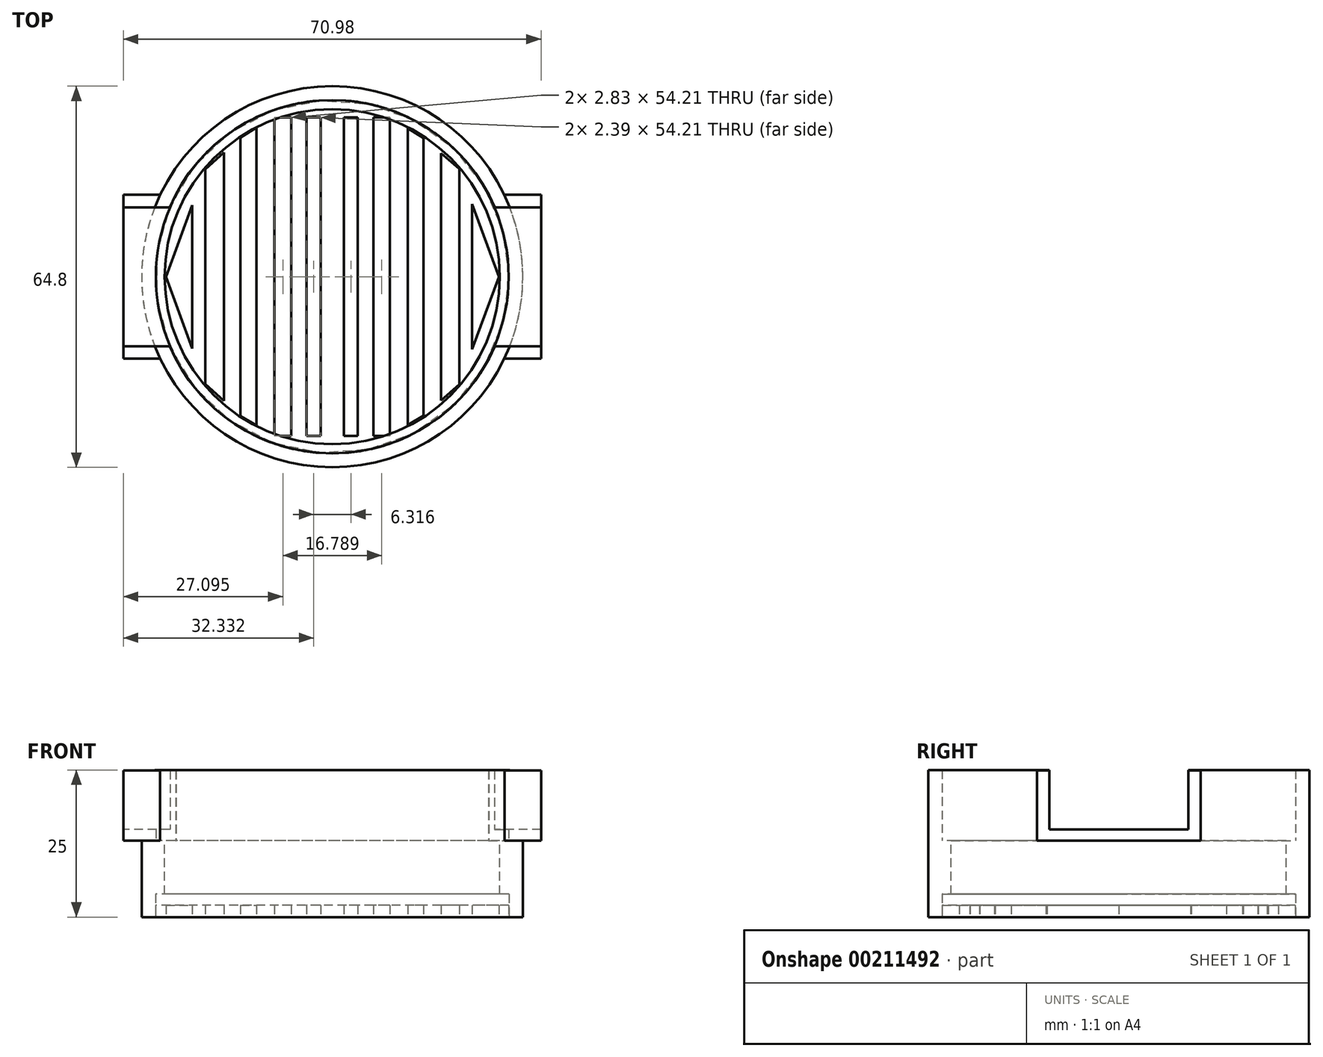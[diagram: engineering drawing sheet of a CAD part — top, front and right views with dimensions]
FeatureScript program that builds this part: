
annotation { "Feature Type Name" : "Feature", "Feature Type Description" : "" }
export const myFeature = defineFeature(function(context is Context, id is Id, definition is map)
    precondition{}
    {
        {
            var Q0;
            Q0=qCreatedBy(makeId("Top.planeOp"),FACE);
            var sketch = newSketch(context, id + "F0", { "sketchPlane" : qUnion([Q0])});
            skCircle(sketch, "E0", {"center": v(0, 0) * mm, "radius": 30 * mm});
            skLineSegment(sketch, "E1.top", {"start": v(1.96, -29.94) * mm, "end": v(-1.96, -29.94) * mm});
            skLineSegment(sketch, "E2.top", {"start": v(-6.98, -29.18) * mm, "end": v(-4.35, -29.18) * mm});
            skPoint(sketch, "E2.middle", {"position": v(-5.67, 0) * mm});
            skLineSegment(sketch, "E3.top", {"start": v(6.98, -29.18) * mm, "end": v(4.35, -29.18) * mm});
            skPoint(sketch, "E3.middle", {"position": v(5.67, 0) * mm});
            skLineSegment(sketch, "E4.top", {"start": v(-12.86, -27.1) * mm, "end": v(-9.8, -27.1) * mm});
            skLineSegment(sketch, "E4.right", {"start": v(-9.8, 27.1) * mm, "end": v(-9.8, -27.1) * mm});
            skPoint(sketch, "E4.middle", {"position": v(-11.33, 0) * mm});
            skLineSegment(sketch, "E5.top", {"start": v(12.86, -27.1) * mm, "end": v(9.8, -27.1) * mm});
            skLineSegment(sketch, "E5.right", {"start": v(9.8, 27.1) * mm, "end": v(9.8, -27.1) * mm});
            skPoint(sketch, "E5.middle", {"position": v(11.33, 0) * mm});
            skPoint(sketch, "E5.cornerSnap0", {"position": v(-11.33, 27.1) * mm});
            skPoint(sketch, "E6.middle", {"position": v(-17, 0) * mm});
            skPoint(sketch, "E7.middle", {"position": v(17, 0) * mm});
            skPoint(sketch, "E8.middle", {"position": v(22.67, 0) * mm});
            skPoint(sketch, "E9.middle", {"position": v(-22.67, 0) * mm});
            skLineSegment(sketch, "E10.top", {"start": v(-18.41, -23.69) * mm, "end": v(-15.6, -23.69) * mm});
            skLineSegment(sketch, "E10.right", {"start": v(-15.6, 23.69) * mm, "end": v(-15.6, -23.69) * mm});
            skLineSegment(sketch, "E11.top", {"start": v(-23.8, -18.28) * mm, "end": v(-21.55, -18.28) * mm});
            skLineSegment(sketch, "E11.right", {"start": v(-21.55, 18.28) * mm, "end": v(-21.55, -18.28) * mm});
            skLineSegment(sketch, "E12.top", {"start": v(18.49, -23.63) * mm, "end": v(15.52, -23.63) * mm});
            skLineSegment(sketch, "E12.right", {"start": v(15.52, 23.63) * mm, "end": v(15.52, -23.63) * mm});
            skLineSegment(sketch, "E13.top", {"start": v(23.77, -18.3) * mm, "end": v(21.57, -18.3) * mm});
            skLineSegment(sketch, "E13.right", {"start": v(21.57, 18.3) * mm, "end": v(21.57, -18.3) * mm});
            skLineSegment(sketch, "E14", {"start": v(21.57, -18.3) * mm, "end": v(15.52, -23.63) * mm});
            skLineSegment(sketch, "E15", {"start": v(15.52, -23.63) * mm, "end": v(9.8, -27.1) * mm});
            skLineSegment(sketch, "E16", {"start": v(9.8, -27.1) * mm, "end": v(-9.8, -27.1) * mm});
            skLineSegment(sketch, "E17", {"start": v(-15.6, -23.69) * mm, "end": v(-9.8, -27.1) * mm});
            skLineSegment(sketch, "E18", {"start": v(-15.6, -23.69) * mm, "end": v(-21.55, -18.28) * mm});
            skPoint(sketch, "E19.endSnap0", {"position": v(-12.86, 0) * mm});
            skLineSegment(sketch, "E20", {"start": v(23.77, -12.35) * mm, "end": v(23.77, 12.35) * mm});
            skLineSegment(sketch, "E21", {"start": v(28.3, 0) * mm, "end": v(23.77, 12.35) * mm});
            skLineSegment(sketch, "E22", {"start": v(28.3, 0) * mm, "end": v(23.77, -12.35) * mm});
            skLineSegment(sketch, "E23", {"start": v(18.49, 21.02) * mm, "end": v(18.49, -21.02) * mm});
            skLineSegment(sketch, "E24", {"start": v(12.86, 25.24) * mm, "end": v(12.86, -25.24) * mm});
            skLineSegment(sketch, "E25", {"start": v(6.98, 27.1) * mm, "end": v(6.98, -27.1) * mm});
            skLineSegment(sketch, "E26", {"start": v(-23.8, 12.19) * mm, "end": v(-23.8, -12.19) * mm});
            skLineSegment(sketch, "E27", {"start": v(-18.41, 21.13) * mm, "end": v(-18.41, -21.13) * mm});
            skLineSegment(sketch, "E28", {"start": v(-12.86, 25.4) * mm, "end": v(-12.86, -25.3) * mm});
            skPoint(sketch, "E28.startSnap0", {"position": v(-12.7, 25.4) * mm});
            skLineSegment(sketch, "E29", {"start": v(-6.98, 27.1) * mm, "end": v(-6.98, -27.1) * mm});
            skLineSegment(sketch, "E30", {"start": v(-1.96, -27.1) * mm, "end": v(-1.96, 27.1) * mm});
            skLineSegment(sketch, "E31", {"start": v(1.96, 27.1) * mm, "end": v(1.96, -27.1) * mm});
            skLineSegment(sketch, "E32", {"start": v(-28.27, 0) * mm, "end": v(-23.8, 12.19) * mm});
            skLineSegment(sketch, "E33", {"start": v(-28.27, 0) * mm, "end": v(-23.8, -12.19) * mm});
            skLineSegment(sketch, "E34", {"start": v(21.57, 18.3) * mm, "end": v(18.49, 21.02) * mm});
            skLineSegment(sketch, "E35", {"start": v(-21.55, 18.28) * mm, "end": v(-18.41, 21.13) * mm});
            skLineSegment(sketch, "E36", {"start": v(15.52, 23.63) * mm, "end": v(12.86, 25.24) * mm});
            skLineSegment(sketch, "E37", {"start": v(-15.6, 23.69) * mm, "end": v(-12.86, 25.4) * mm});
            skLineSegment(sketch, "E38", {"start": v(9.8, 27.1) * mm, "end": v(6.98, 27.1) * mm});
            skLineSegment(sketch, "E39", {"start": v(-9.8, 27.1) * mm, "end": v(-6.98, 27.1) * mm});
            skLineSegment(sketch, "E40", {"start": v(4.35, 27.1) * mm, "end": v(1.96, 27.1) * mm});
            skLineSegment(sketch, "E41", {"start": v(-1.96, 27.1) * mm, "end": v(-4.35, 27.1) * mm});
            skLineSegment(sketch, "E42", {"start": v(4.35, 27.1) * mm, "end": v(4.35, -27.1) * mm});
            skLineSegment(sketch, "E43", {"start": v(-4.35, 27.1) * mm, "end": v(-4.35, -27.1) * mm});
            skSolve(sketch);
        }
        {
            var Q0;
            Q0 = qSketchRegion(id + "F0", true);
            extrude(context, id + "F1", {"entities" : qUnion([Q0]), "depth" : 2 * mm});
        }
        {
            var Q0;
            Q0=qCreatedBy(makeId("Top.planeOp"),FACE);
            var sketch = newSketch(context, id + "F2", { "sketchPlane" : qUnion([Q0])});
            skCircle(sketch, "E44", {"center": v(0, 0) * mm, "radius": 30.04 * mm});
            skCircle(sketch, "E45", {"center": v(0, 0) * mm, "radius": 32.4 * mm});
            skSolve(sketch);
        }
        {
            var Q0;
            Q0 = qSketchRegion(id + "F2", true);
            extrude(context, id + "F3", {"entities" : qUnion([Q0]), "depth" : 25 * mm});
        }
        {
            var Q0;
            Q0=qCreatedBy(makeId("Top.planeOp"),FACE);
            cPlane(context, id + "F4", {"entities" : qUnion([Q0]), "cplaneType" : CPlaneType.OFFSET, "offset" : 13 * mm, "width" : 150 * mm, "height" : 150 * mm});
        }
        {
            var Q0;
            Q0=qCreatedBy(id+"F4.planeOp",FACE);
            var sketch = newSketch(context, id + "F5", { "sketchPlane" : qUnion([Q0])});
            skLineSegment(sketch, "E46.bottom", {"start": v(-35.49, 13.92) * mm, "end": v(35.49, 13.92) * mm});
            skLineSegment(sketch, "E46.top", {"start": v(-35.49, -13.92) * mm, "end": v(35.49, -13.92) * mm});
            skLineSegment(sketch, "E46.left", {"start": v(-35.49, 13.92) * mm, "end": v(-35.49, -13.92) * mm});
            skLineSegment(sketch, "E46.right", {"start": v(35.49, 13.92) * mm, "end": v(35.49, -13.92) * mm});
            skPoint(sketch, "E46.middle", {"position": v(0, 0) * mm});
            skSolve(sketch);
        }
        {
            var Q0;
            Q0 = qSketchRegion(id + "F5", true);
            extrude(context, id + "F6", {"entities" : qUnion([Q0]), "operationType" : NewBodyOperationType.ADD, "depth" : 11.9 * mm});
        }
        {
            var Q0;
            Q0=qCreatedBy(makeId("Right.planeOp"),FACE);
            var sketch = newSketch(context, id + "F7", { "sketchPlane" : qUnion([Q0])});
            skLineSegment(sketch, "E47.bottom", {"start": v(11.81, 14.9) * mm, "end": v(-11.81, 14.9) * mm});
            skLineSegment(sketch, "E47.top", {"start": v(11.81, 44.48) * mm, "end": v(-11.81, 44.48) * mm});
            skLineSegment(sketch, "E47.left", {"start": v(11.81, 14.9) * mm, "end": v(11.81, 44.48) * mm});
            skLineSegment(sketch, "E47.right", {"start": v(-11.81, 14.9) * mm, "end": v(-11.81, 44.48) * mm});
            skPoint(sketch, "E47.middle", {"position": v(0, 29.69) * mm});
            skSolve(sketch);
        }
        {
            var Q0;
            Q0 = qSketchRegion(id + "F7", true);
            extrude(context, id + "F8", {"entities" : qUnion([Q0]), "operationType" : NewBodyOperationType.REMOVE, "endBound" : BoundingType.SYMMETRIC, "depth" : 140.4 * mm});
        }
        {
            var Q0;
            Q0=qCreatedBy(id+"F4.planeOp",FACE);
            var sketch = newSketch(context, id + "F9", { "sketchPlane" : qUnion([Q0])});
            skCircle(sketch, "E48", {"center": v(0, 0) * mm, "radius": 29.98 * mm});
            skSolve(sketch);
        }
        {
            var Q0;
            Q0 = qSketchRegion(id + "F9", true);
            extrude(context, id + "F10", {"entities" : qUnion([Q0]), "operationType" : NewBodyOperationType.REMOVE, "depth" : 61.4 * mm});
        }
        {
            var Q0;
            Q0=qCreatedBy(id+"F4.planeOp",FACE);
            var sketch = newSketch(context, id + "F11", { "sketchPlane" : qUnion([Q0])});
            skCircle(sketch, "E49", {"center": v(0, 0) * mm, "radius": 30.04 * mm});
            skCircle(sketch, "E50", {"center": v(0, 0) * mm, "radius": 28.48 * mm});
            skSolve(sketch);
        }
        {
            var Q0;
            Q0 = qSketchRegion(id + "F11", true);
            extrude(context, id + "F12", {"entities" : qUnion([Q0]), "operationType" : NewBodyOperationType.ADD, "oppositeDirection" : true, "depth" : 9.1 * mm});
        }
    });
